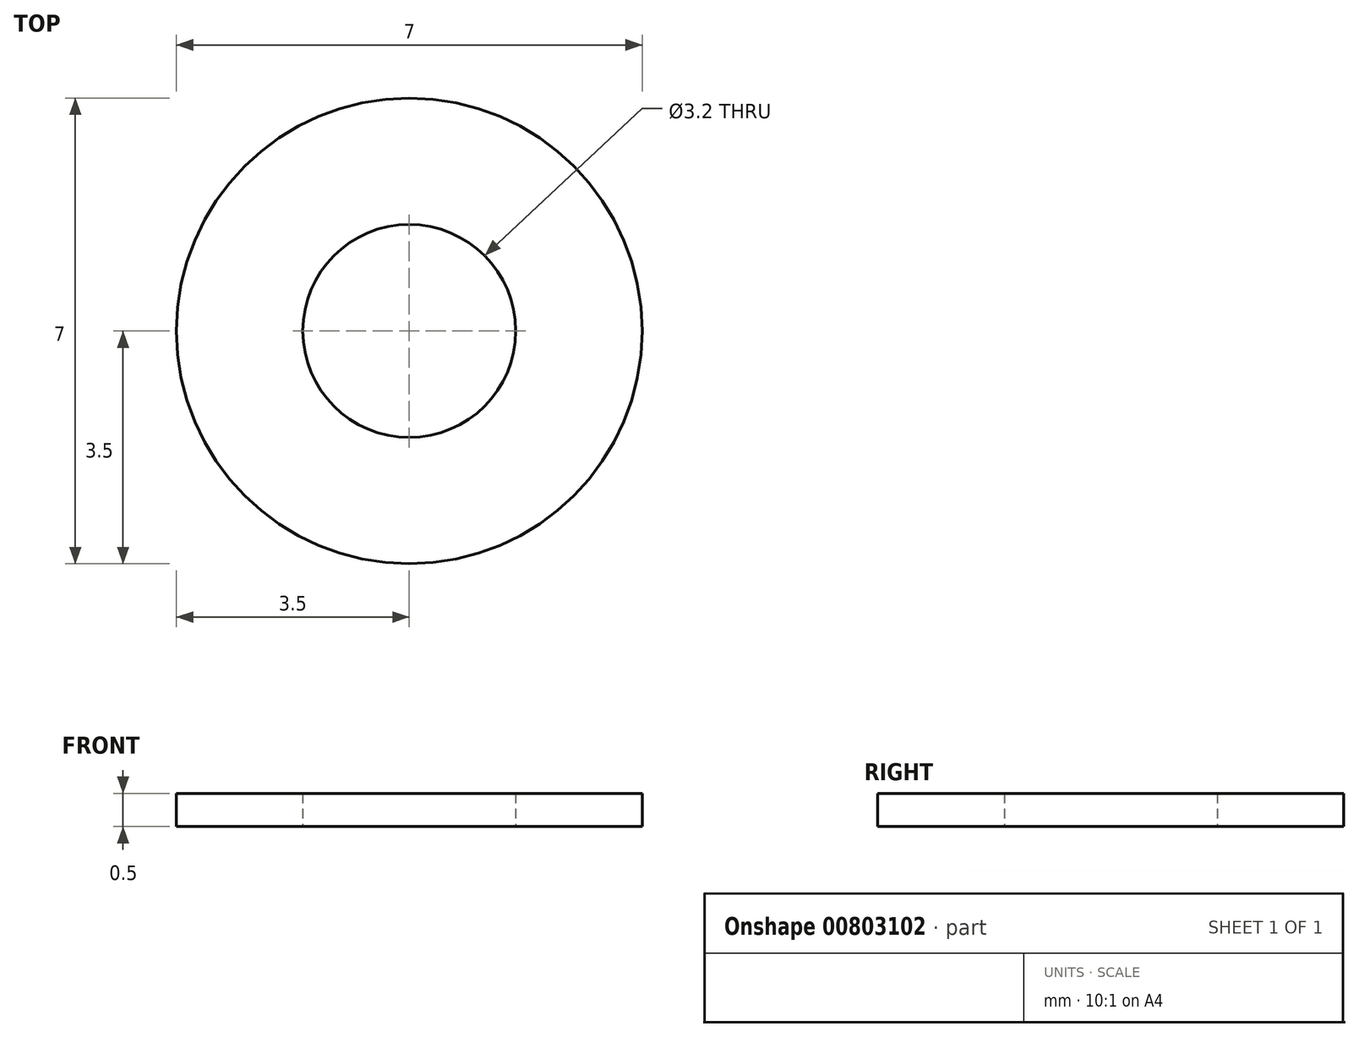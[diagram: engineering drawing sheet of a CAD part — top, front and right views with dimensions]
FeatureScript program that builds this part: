
annotation { "Feature Type Name" : "Feature", "Feature Type Description" : "" }
export const myFeature = defineFeature(function(context is Context, id is Id, definition is map)
    precondition{}
    {
        {
            var Q0;
            Q0=qCreatedBy(makeId("Top.planeOp"),FACE);
            var sketch = newSketch(context, id + "F0", { "sketchPlane" : qUnion([Q0])});
            skCircle(sketch, "E0", {"center": v(0, 0) * mm, "radius": 3.5 * mm});
            skCircle(sketch, "E1", {"center": v(0, 0) * mm, "radius": 1.6 * mm});
            skSolve(sketch);
        }
        {
            var Q0;
            Q0=makeQuery(id+"F0.imprint","IMPRINT",FACE,{"disambiguationData":[TD([[makeQuery(id+"F0.imprint","IMPRINT",EDGE,{"derivedFrom":sQuery(id+"F0.wireOp",EDGE,"E0")}),1.0]])]});
            extrude(context, id + "F1", {"entities" : qUnion([Q0]), "depth" : 0.5 * mm, "offsetDistance" : 25 * mm});
        }
    });
